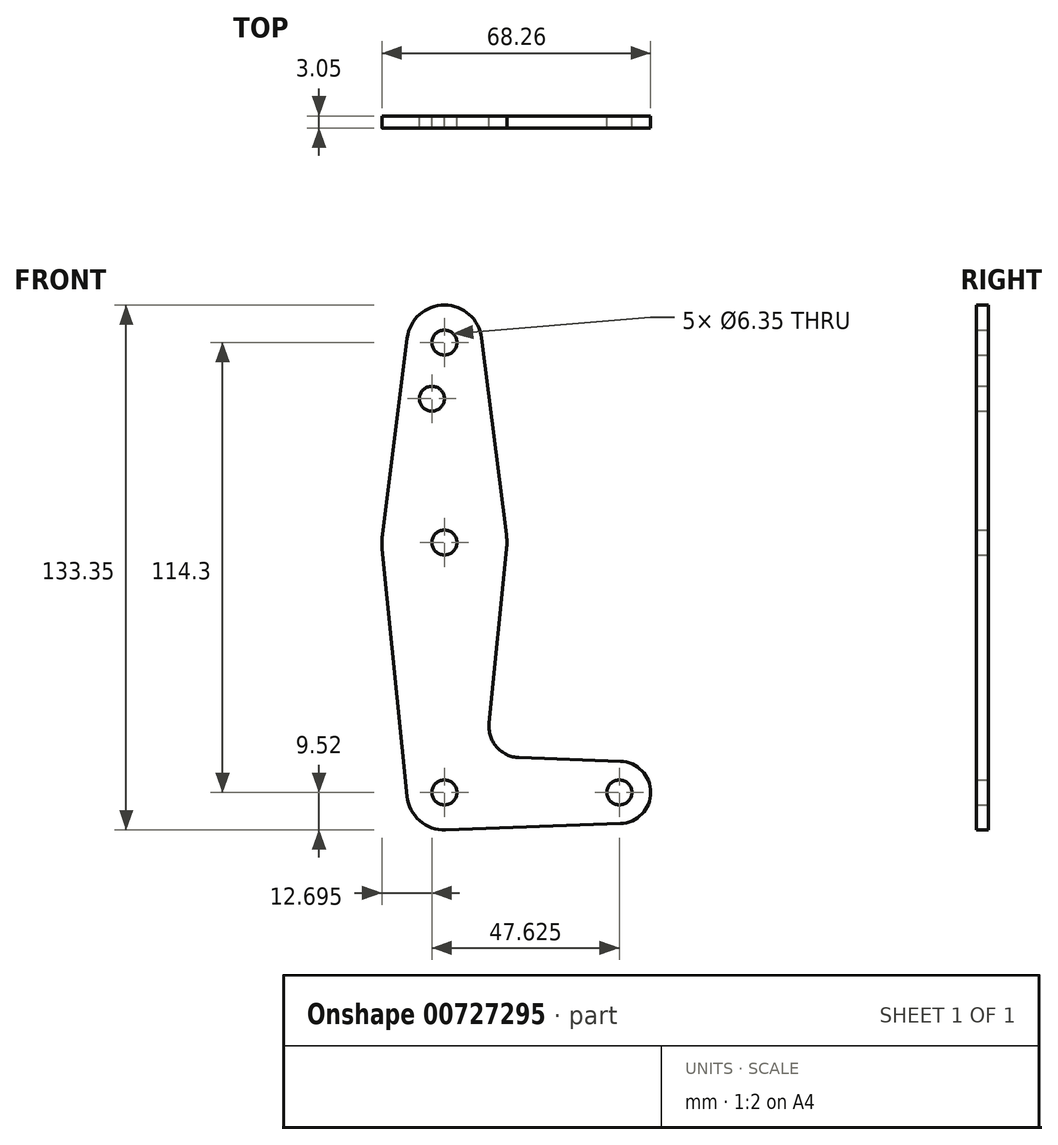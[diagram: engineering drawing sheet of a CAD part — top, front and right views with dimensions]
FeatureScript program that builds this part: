
annotation { "Feature Type Name" : "Feature", "Feature Type Description" : "" }
export const myFeature = defineFeature(function(context is Context, id is Id, definition is map)
    precondition{}
    {
        {
            var Q0;
            Q0=qCreatedBy(makeId("Front.planeOp"),FACE);
            var sketch = newSketch(context, id + "F0", { "sketchPlane" : qUnion([Q0])});
            skLineSegment(sketch, "E0", {"start": v(0, 0) * mm, "end": v(0, 114.3) * mm, "construction": true});
            skLineSegment(sketch, "E1", {"start": v(0, 0) * mm, "end": v(44.45, 0) * mm, "construction": true});
            skCircle(sketch, "E2", {"center": v(0, 0) * mm, "radius": 9.53 * mm});
            skCircle(sketch, "E3", {"center": v(44.45, 0) * mm, "radius": 7.94 * mm});
            skCircle(sketch, "E4", {"center": v(0, 114.3) * mm, "radius": 9.53 * mm});
            skCircle(sketch, "E5", {"center": v(0, 63.5) * mm, "radius": 15.88 * mm});
            skLineSegment(sketch, "E6", {"start": v(-9.45, 115.5) * mm, "end": v(-15.75, 65.48) * mm});
            skLineSegment(sketch, "E7", {"start": v(9.45, 115.5) * mm, "end": v(15.75, 65.48) * mm});
            skLineSegment(sketch, "E8", {"start": v(-15.8, 61.91) * mm, "end": v(-9.48, -0.95) * mm});
            skLineSegment(sketch, "E9", {"start": v(15.8, 61.91) * mm, "end": v(11.34, 17.6) * mm});
            skLineSegment(sketch, "E10", {"start": v(18.97, 8.85) * mm, "end": v(44.73, 7.93) * mm});
            skLineSegment(sketch, "E11", {"start": v(0.34, -9.52) * mm, "end": v(44.73, -7.93) * mm});
            skArc(sketch, "E12.filletArc", {"start": v(11.34, 17.6) * mm, "mid": v(13.26, 11.57) * mm, "end": v(18.97, 8.85) * mm});
            skCircle(sketch, "E13", {"center": v(0, 114.3) * mm, "radius": 3.18 * mm});
            skCircle(sketch, "E14", {"center": v(0, 63.5) * mm, "radius": 3.18 * mm});
            skCircle(sketch, "E15", {"center": v(0, 0) * mm, "radius": 3.18 * mm});
            skCircle(sketch, "E16", {"center": v(44.45, 0) * mm, "radius": 3.18 * mm});
            skCircle(sketch, "E17", {"center": v(-3.18, 100.03) * mm, "radius": 3.18 * mm});
            skSolve(sketch);
        }
        {
            var Q0;
            Q0 = qSketchRegion(id + "F0", true);
            extrude(context, id + "F1", {"entities" : qUnion([Q0]), "depth" : 3.05 * mm, "offsetDistance" : 25.4 * mm});
        }
    });
